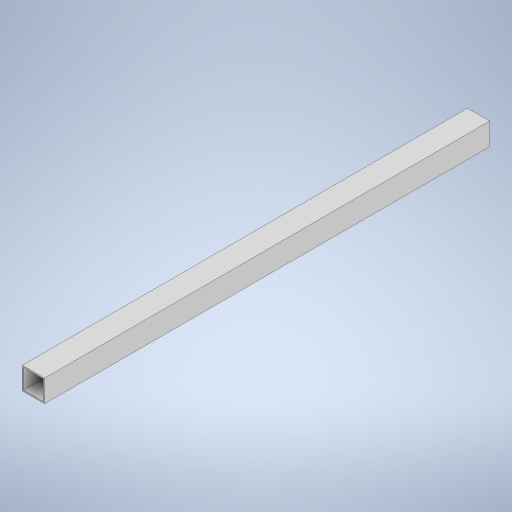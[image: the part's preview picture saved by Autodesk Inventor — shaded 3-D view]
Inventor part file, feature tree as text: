
AUTODESK INVENTOR PART (.ipt)
format: ipt  version: 2024 (Build 280153000, 153)  size: 234,496 bytes
history: native  units: in
note: dims shown in document units (in); Inventor stores cm internally (conversion verified against a paired STEP export)
features: extrude x1, sketch x1
ambient origin geometry x8: Origin, YZ Plane, XZ Plane, XY Plane, X Axis, Y Axis, Z Axis, Center Point
bodies: Solid1 (feature_tree)
feature tree (2):
  extrude  "Extrusion1"  Depth=1.0in
  sketch  "Sketch1"  dims[d0=1.0in d1=1.0in d2=0.0625in d3=20.0in d4=0.0in]
